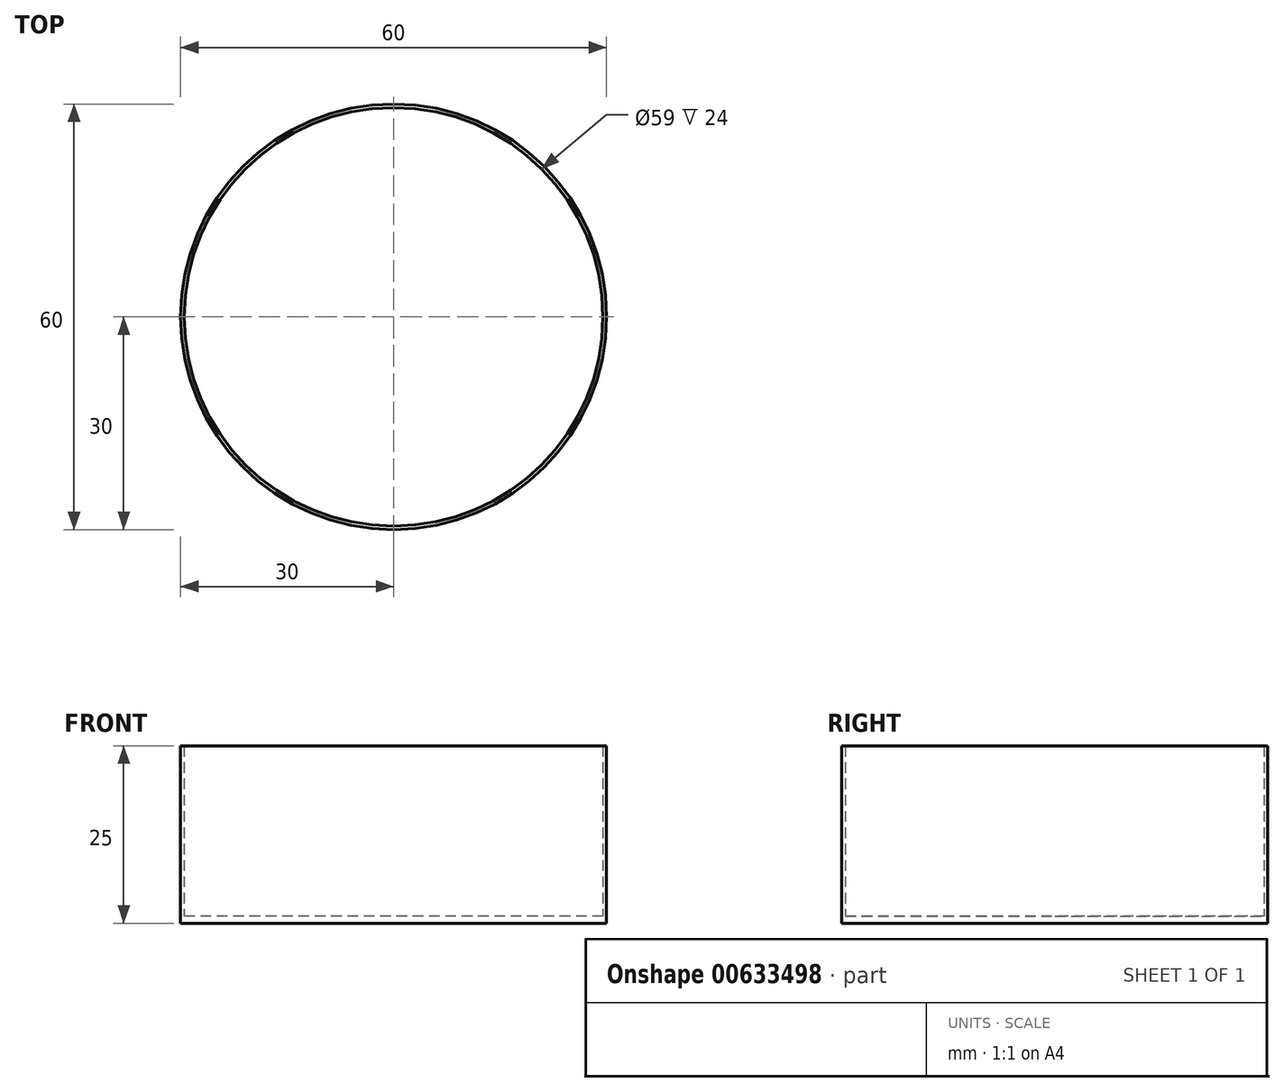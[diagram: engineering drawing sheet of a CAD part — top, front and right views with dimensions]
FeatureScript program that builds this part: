
annotation { "Feature Type Name" : "Feature", "Feature Type Description" : "" }
export const myFeature = defineFeature(function(context is Context, id is Id, definition is map)
    precondition{}
    {
        {
            var Q0;
            Q0=qCreatedBy(makeId("Front.planeOp"),FACE);
            var sketch = newSketch(context, id + "F0", { "sketchPlane" : qUnion([Q0])});
            skLineSegment(sketch, "E0", {"start": v(0, -10.4) * mm, "end": v(0, 14.6) * mm, "construction": true});
            skLineSegment(sketch, "E1", {"start": v(0, -10.4) * mm, "end": v(30, -10.4) * mm});
            skLineSegment(sketch, "E2", {"start": v(30, -10.4) * mm, "end": v(30, -9.4) * mm});
            skLineSegment(sketch, "E3", {"start": v(30, -9.4) * mm, "end": v(0, -9.4) * mm});
            skLineSegment(sketch, "E4", {"start": v(0, -9.4) * mm, "end": v(0, -10.4) * mm});
            skSolve(sketch);
        }
        {
            var Q0;
            Q0=makeQuery(id+"F0.imprint","IMPRINT",FACE,{"disambiguationData":[TD([[makeQuery(id+"F0.imprint","IMPRINT",EDGE,{"derivedFrom":sQuery(id+"F0.wireOp",EDGE,"E1")}),1.0]])]});
            var Q1;
            Q1=sQuery(id+"F0.wireOp",EDGE,"E0");
            revolve(context, id + "F1", {"entities" : qUnion([Q0]), "axis" : qUnion([Q1]), "revolveType" : RevolveType.FULL});
        }
        {
            var Q0;
            Q0=makeQuery(id+"F1.opRevolve","SWEPT_FACE",FACE,{"disambiguationData":[OSD([sQuery(id+"F0.wireOp",EDGE,"E3")])]});
            var sketch = newSketch(context, id + "F2", { "sketchPlane" : qUnion([Q0])});
            skCircle(sketch, "E5.0", {"center": v(0, 0) * mm, "radius": 29.5 * mm});
            skSolve(sketch);
        }
        {
            var Q0;
            Q0=makeQuery(id+"F2.imprint","IMPRINT",FACE,{"disambiguationData":[TD([[makeQuery(id+"F2.imprint","IMPRINT",EDGE,{"derivedFrom":sQuery(id+"F2.wireOp",EDGE,"E5.0")}),-1.0]])]});
            extrude(context, id + "F3", {"entities" : qUnion([Q0]), "operationType" : NewBodyOperationType.ADD, "depth" : 24 * mm, "offsetDistance" : 25 * mm});
        }
    });
